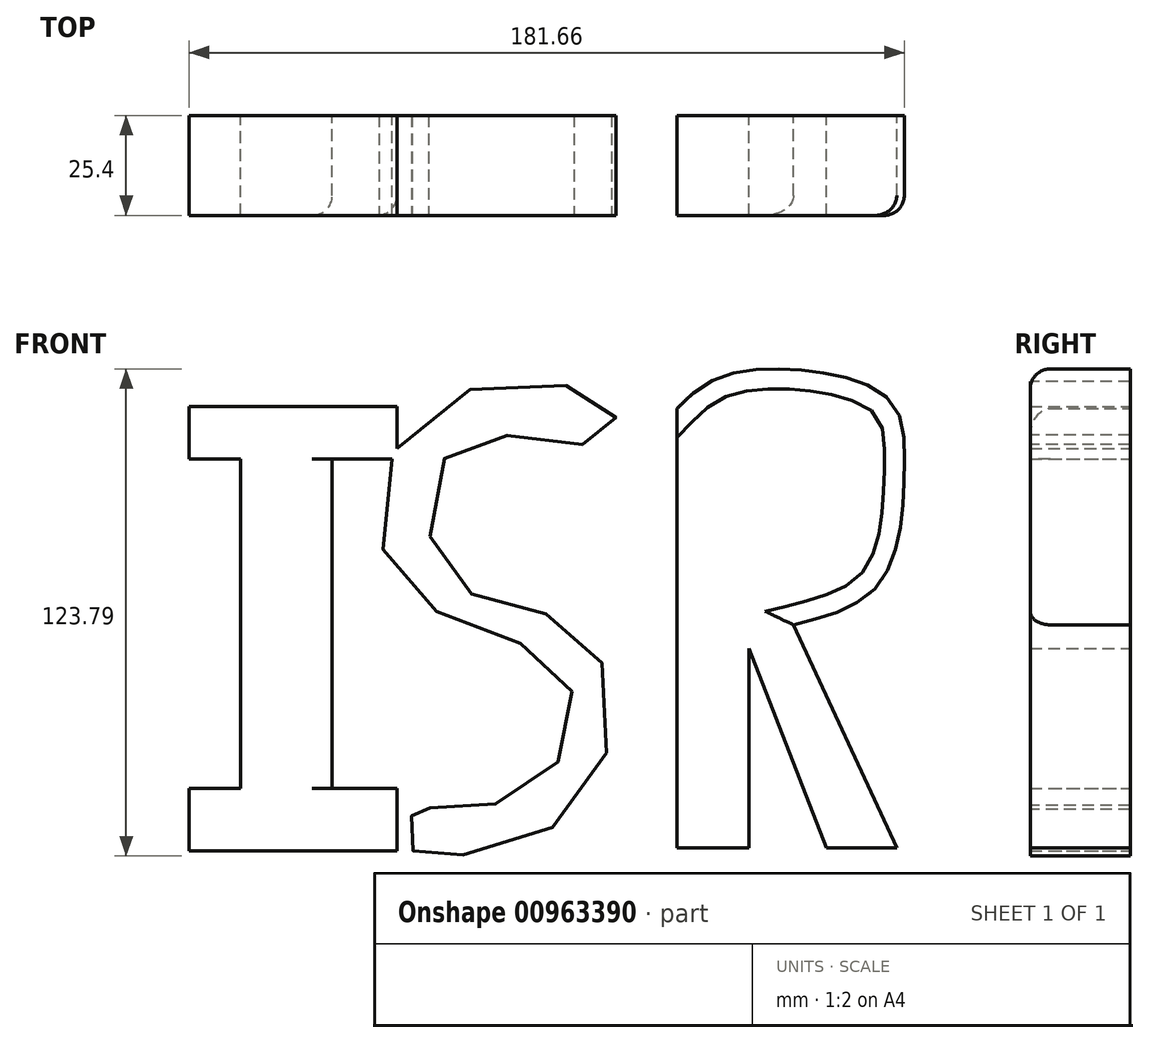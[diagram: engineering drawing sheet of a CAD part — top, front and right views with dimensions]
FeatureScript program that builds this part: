
annotation { "Feature Type Name" : "Feature", "Feature Type Description" : "" }
export const myFeature = defineFeature(function(context is Context, id is Id, definition is map)
    precondition{}
    {
        {
            var Q0;
            Q0=qCreatedBy(makeId("Front.planeOp"),FACE);
            var sketch = newSketch(context, id + "F0", { "sketchPlane" : qUnion([Q0])});
            skLineSegment(sketch, "E0.bottom", {"start": v(-54.52, 42.13) * mm, "end": v(-31.2, 42.13) * mm});
            skLineSegment(sketch, "E0.top", {"start": v(-54.52, -41.55) * mm, "end": v(-31.2, -41.55) * mm});
            skLineSegment(sketch, "E0.left", {"start": v(-54.52, 42.13) * mm, "end": v(-54.52, -41.55) * mm});
            skLineSegment(sketch, "E0.right", {"start": v(-31.2, 42.13) * mm, "end": v(-31.2, -41.55) * mm});
            skLineSegment(sketch, "E1.bottom", {"start": v(-67.51, -41.55) * mm, "end": v(-14.76, -41.55) * mm});
            skLineSegment(sketch, "E1.top", {"start": v(-67.51, -57.37) * mm, "end": v(-14.76, -57.37) * mm});
            skLineSegment(sketch, "E1.left", {"start": v(-67.51, -41.55) * mm, "end": v(-67.51, -57.37) * mm});
            skLineSegment(sketch, "E1.right", {"start": v(-14.76, -41.55) * mm, "end": v(-14.76, -57.37) * mm});
            skLineSegment(sketch, "E2.bottom", {"start": v(-14.76, 42.13) * mm, "end": v(-67.53, 42.13) * mm});
            skLineSegment(sketch, "E2.top", {"start": v(-14.76, 55.44) * mm, "end": v(-67.53, 55.44) * mm});
            skLineSegment(sketch, "E2.left", {"start": v(-14.76, 42.13) * mm, "end": v(-14.76, 55.44) * mm});
            skLineSegment(sketch, "E2.right", {"start": v(-67.53, 42.13) * mm, "end": v(-67.53, 55.44) * mm});
            skFitSpline(sketch, "E3", {"points": [v(35.27, 46.2) * mm, v(1.05, 46.14) * mm, v(-1.92, 12.18) * mm, v(32.27, -2.11) * mm, v(30.13, -47.44) * mm, v(-9.9, -58) * mm, v(-10.9, -55.46) * mm, v(-10.7, -46.31) * mm, v(-8.25, -46.22) * mm, v(20.3, -41.08) * mm, v(27.15, -11.74) * mm, v(-13.98, 10.49) * mm, v(-4.82, 55.82) * mm, v(40, 54.95) * mm, v(35.27, 46.2) * mm]});
            skLineSegment(sketch, "E4", {"start": v(56.4, 54.95) * mm, "end": v(56.4, -56.63) * mm});
            skLineSegment(sketch, "E5", {"start": v(56.4, -56.63) * mm, "end": v(74.7, -56.63) * mm});
            skLineSegment(sketch, "E6", {"start": v(74.7, -56.63) * mm, "end": v(74.7, -5.94) * mm});
            skLineSegment(sketch, "E7", {"start": v(74.7, -5.94) * mm, "end": v(94.42, -56.63) * mm});
            skLineSegment(sketch, "E8", {"start": v(94.42, -56.63) * mm, "end": v(112.25, -56.63) * mm});
            skLineSegment(sketch, "E9", {"start": v(112.25, -56.63) * mm, "end": v(85.97, 0) * mm});
            skFitSpline(sketch, "E10", {"points": [v(85.97, 0) * mm, v(108.5, 11.43) * mm, v(114.13, 41.93) * mm, v(108.5, 58.83) * mm, v(70.95, 64) * mm, v(56.4, 54.95) * mm], "startDerivative": vector(138.19, 34.62) * mm, "endDerivative": vector(-64.25, -66.56) * mm});
            skSolve(sketch);
        }
        {
            var Q0;
            Q0 = qSketchRegion(id + "F0", true);
            extrude(context, id + "F1", {"entities" : qUnion([Q0]), "depth" : 25.4 * mm, "offsetDistance" : 25.4 * mm});
        }
        {
            var Q0;
            Q0=makeQuery(id+"F1.opExtrude","CAP_FACE",FACE,{"disambiguationData":[OSD([sQuery(id+"F0.wireOp",EDGE,"E4"),sQuery(id+"F0.wireOp",EDGE,"E5"),sQuery(id+"F0.wireOp",EDGE,"E6"),sQuery(id+"F0.wireOp",EDGE,"E7"),sQuery(id+"F0.wireOp",EDGE,"E8"),sQuery(id+"F0.wireOp",EDGE,"E9"),sQuery(id+"F0.wireOp",EDGE,"E10")])],"isStart":false});
            var sketch = newSketch(context, id + "F2", { "sketchPlane" : qUnion([Q0])});
            skFitSpline(sketch, "E11", {"points": [v(70.87, 44.04) * mm, v(77.12, 49.34) * mm, v(94.25, 50.06) * mm, v(102.03, 44.36) * mm, v(102.68, 24.25) * mm, v(93.25, 14.78) * mm, v(72.2, 17.6) * mm, v(70.87, 44.04) * mm]});
            skSolve(sketch);
        }
        {
            var Q0;
            Q0=makeQuery(id+"F2.imprint","IMPRINT",FACE,{"disambiguationData":[TD([[makeQuery(id+"F2.imprint","IMPRINT",EDGE,{"derivedFrom":sQuery(id+"F2.wireOp",EDGE,"E11")}),-1.0]])]});
            extrude(context, id + "F3", {"entities" : qUnion([Q0]), "operationType" : NewBodyOperationType.ADD, "depth" : -25.4 * mm, "offsetDistance" : 25.4 * mm});
        }
        {
            var Q0;
            Q0=makeQuery(id+"F1.opExtrude","CAP_EDGE",EDGE,{"disambiguationData":[OSD([sQuery(id+"F0.wireOp",EDGE,"E0.right")])],"isStart":false});
            var Q1;
            Q1=makeQuery(id+"F1.opExtrude","CAP_EDGE",EDGE,{"disambiguationData":[OSD([sQuery(id+"F0.wireOp",EDGE,"E1.right")])],"isStart":false});
            var Q2;
            Q2=makeQuery(id+"F1.opExtrude","CAP_EDGE",EDGE,{"disambiguationData":[OSD([sQuery(id+"F0.wireOp",EDGE,"E10")])],"isStart":false});
            var Q3;
            Q3=makeQuery(id+"F1.opExtrude","CAP_EDGE",EDGE,{"disambiguationData":[OSD([sQuery(id+"F0.wireOp",EDGE,"E9")])],"isStart":false});
            fillet(context, id + "F4", {"entities" : qUnion([Q0, Q1, Q2, Q3]), "radius" : 5.08 * mm, "tangentPropagation" : true, "allowEdgeOverflow" : false});
        }
    });
